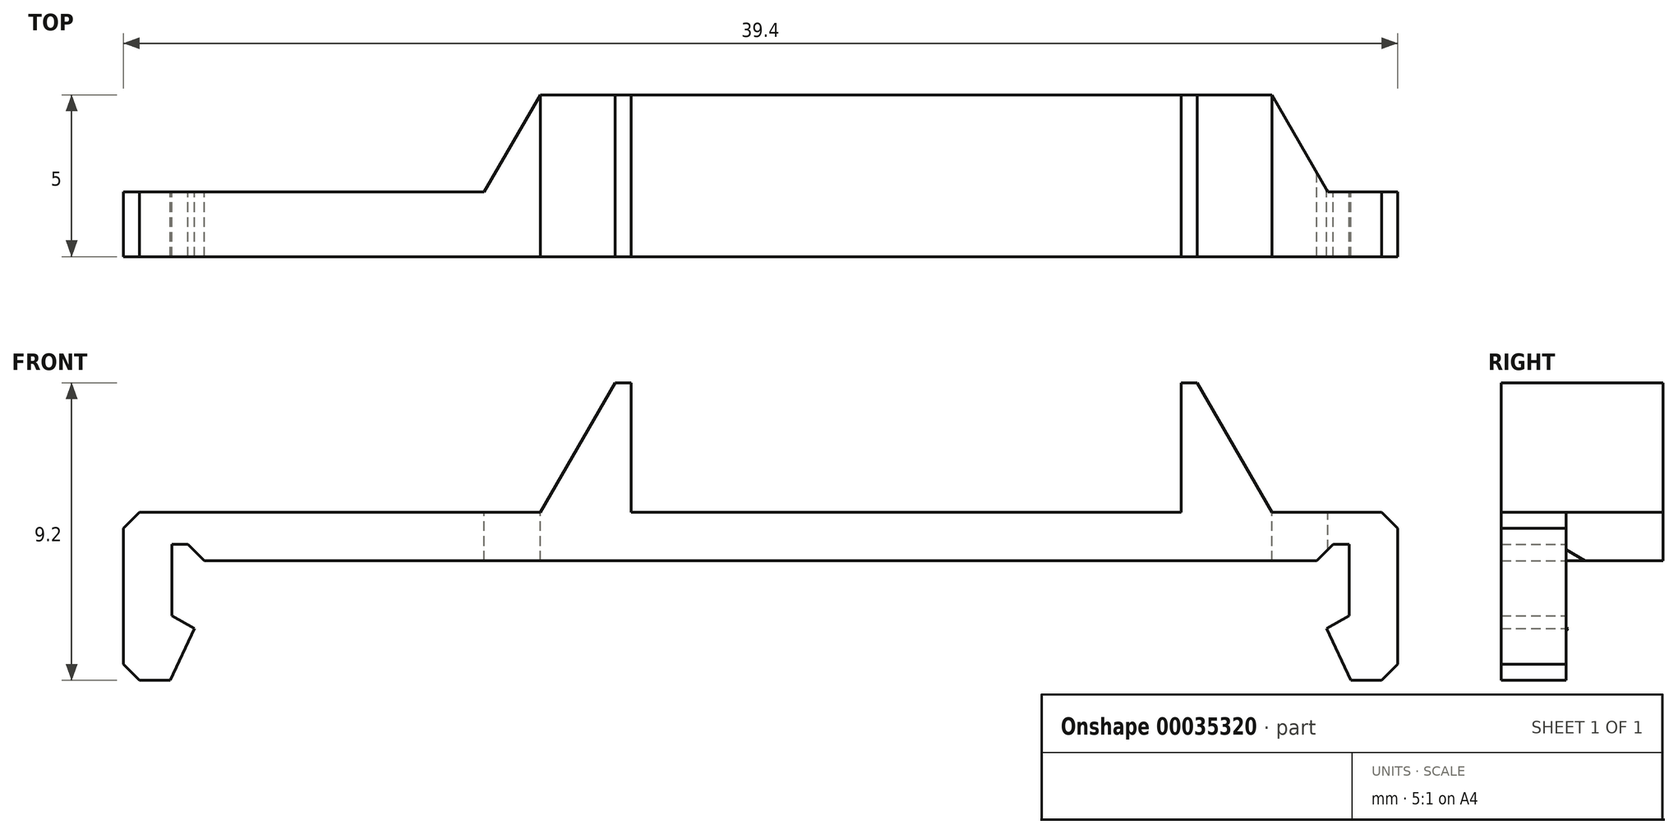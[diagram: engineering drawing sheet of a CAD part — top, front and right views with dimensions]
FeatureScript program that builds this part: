
annotation { "Feature Type Name" : "Feature", "Feature Type Description" : "" }
export const myFeature = defineFeature(function(context is Context, id is Id, definition is map)
    precondition{}
    {
        {
            var Q0;
            Q0=qCreatedBy(makeId("Front.planeOp"),FACE);
            var sketch = newSketch(context, id + "F0", { "sketchPlane" : qUnion([Q0])});
            skLineSegment(sketch, "E0", {"start": v(-18.2, 0) * mm, "end": v(-18.2, -1.7) * mm});
            skLineSegment(sketch, "E1", {"start": v(-19.7, -3.2) * mm, "end": v(-19.7, 0) * mm});
            skLineSegment(sketch, "E2", {"start": v(-18.2, 0) * mm, "end": v(-18.2, 0.5) * mm});
            skLineSegment(sketch, "E3", {"start": v(-18.2, 0.5) * mm, "end": v(-17.7, 0.5) * mm});
            skLineSegment(sketch, "E4", {"start": v(-17.7, 0.5) * mm, "end": v(-17.2, 0) * mm});
            skLineSegment(sketch, "E5", {"start": v(-17.2, 0) * mm, "end": v(0, 0) * mm});
            skLineSegment(sketch, "E6", {"start": v(-19.7, 0) * mm, "end": v(-19.7, 1) * mm});
            skLineSegment(sketch, "E7", {"start": v(-19.7, 1) * mm, "end": v(-19.2, 1.5) * mm});
            skLineSegment(sketch, "E8", {"start": v(-19.2, 1.5) * mm, "end": v(0, 1.5) * mm});
            skLineSegment(sketch, "E9", {"start": v(-18.2, -1.7) * mm, "end": v(-17.5, -2.1) * mm});
            skLineSegment(sketch, "E10", {"start": v(-17.5, -2.1) * mm, "end": v(-18.24, -3.7) * mm});
            skLineSegment(sketch, "E11", {"start": v(-18.24, -3.7) * mm, "end": v(-19.2, -3.7) * mm});
            skLineSegment(sketch, "E12", {"start": v(-19.2, -3.7) * mm, "end": v(-19.7, -3.2) * mm});
            skLineSegment(sketch, "E13.MirrorCS", {"start": v(18.2, 0) * mm, "end": v(18.2, 0.5) * mm});
            skLineSegment(sketch, "E14.MirrorCS", {"start": v(18.2, -1.7) * mm, "end": v(17.5, -2.1) * mm});
            skLineSegment(sketch, "E15.MirrorCS", {"start": v(18.2, 0.5) * mm, "end": v(17.7, 0.5) * mm});
            skLineSegment(sketch, "E16.MirrorCS", {"start": v(18.24, -3.7) * mm, "end": v(19.2, -3.7) * mm});
            skLineSegment(sketch, "E17.MirrorCS", {"start": v(17.7, 0.5) * mm, "end": v(17.2, 0) * mm});
            skLineSegment(sketch, "E18.MirrorCS", {"start": v(18.2, 0) * mm, "end": v(18.2, -1.7) * mm});
            skLineSegment(sketch, "E19.MirrorCS", {"start": v(19.7, -3.2) * mm, "end": v(19.7, 0) * mm});
            skLineSegment(sketch, "E20.MirrorCS", {"start": v(17.5, -2.1) * mm, "end": v(18.24, -3.7) * mm});
            skLineSegment(sketch, "E21.MirrorCS", {"start": v(19.2, -3.7) * mm, "end": v(19.7, -3.2) * mm});
            skLineSegment(sketch, "E22.MirrorCS", {"start": v(19.7, 0) * mm, "end": v(19.7, 1) * mm});
            skLineSegment(sketch, "E23.MirrorCS", {"start": v(19.7, 1) * mm, "end": v(19.2, 1.5) * mm});
            skLineSegment(sketch, "E24.MirrorCS", {"start": v(17.2, 0) * mm, "end": v(0, 0) * mm});
            skLineSegment(sketch, "E25.MirrorCS", {"start": v(19.2, 1.5) * mm, "end": v(0, 1.5) * mm});
            skLineSegment(sketch, "E26", {"start": v(-6.8, 1.5) * mm, "end": v(-4.5, 5.5) * mm});
            skLineSegment(sketch, "E27", {"start": v(-4.5, 5.5) * mm, "end": v(-4, 5.5) * mm});
            skLineSegment(sketch, "E28", {"start": v(-4, 5.5) * mm, "end": v(-4, 1.5) * mm});
            skLineSegment(sketch, "E29", {"start": v(4.5, 1.5) * mm, "end": v(4.5, 0) * mm, "construction": true});
            skLineSegment(sketch, "E30.MirrorCS", {"start": v(13, 5.5) * mm, "end": v(13, 1.5) * mm});
            skLineSegment(sketch, "E31.MirrorCS", {"start": v(13.5, 5.5) * mm, "end": v(13, 5.5) * mm});
            skLineSegment(sketch, "E32.MirrorCS", {"start": v(15.8, 1.5) * mm, "end": v(13.5, 5.5) * mm});
            skSolve(sketch);
        }
        {
            var Q0;
            Q0=qCreatedBy(makeId("Top.planeOp"),FACE);
            var sketch = newSketch(context, id + "F1", { "sketchPlane" : qUnion([Q0])});
            skPoint(sketch, "E33.0", {"position": v(-19.7, 0) * mm});
            skPoint(sketch, "E33.1", {"position": v(19.7, 0) * mm});
            skPoint(sketch, "E34.0", {"position": v(15.8, 0) * mm});
            skPoint(sketch, "E34.1", {"position": v(-6.8, 0) * mm});
            skLineSegment(sketch, "E35", {"start": v(-19.7, 0) * mm, "end": v(-19.7, -2) * mm});
            skLineSegment(sketch, "E36", {"start": v(-19.7, -2) * mm, "end": v(19.7, -2) * mm});
            skLineSegment(sketch, "E37", {"start": v(19.7, -2) * mm, "end": v(19.7, 0) * mm});
            skLineSegment(sketch, "E38", {"start": v(19.7, 0) * mm, "end": v(17.54, 0) * mm});
            skLineSegment(sketch, "E39", {"start": v(17.54, 0) * mm, "end": v(15.8, 3) * mm});
            skLineSegment(sketch, "E40", {"start": v(15.8, 3) * mm, "end": v(-6.8, 3) * mm});
            skLineSegment(sketch, "E41", {"start": v(-6.8, 3) * mm, "end": v(-8.54, 0) * mm});
            skLineSegment(sketch, "E42", {"start": v(-8.54, 0) * mm, "end": v(-19.7, 0) * mm});
            skSolve(sketch);
        }
        {
            var Q0;
            Q0 = qSketchRegion(id + "F0", true);
            extrude(context, id + "F2", {"entities" : qUnion([Q0]), "endBound" : BoundingType.SYMMETRIC, "depth" : 25 * mm});
        }
        {
            var Q0;
            Q0 = qSketchRegion(id + "F1", true);
            extrude(context, id + "F3", {"entities" : qUnion([Q0]), "operationType" : NewBodyOperationType.INTERSECT, "endBound" : BoundingType.SYMMETRIC, "oppositeDirection" : true, "depth" : 25 * mm});
        }
    });
